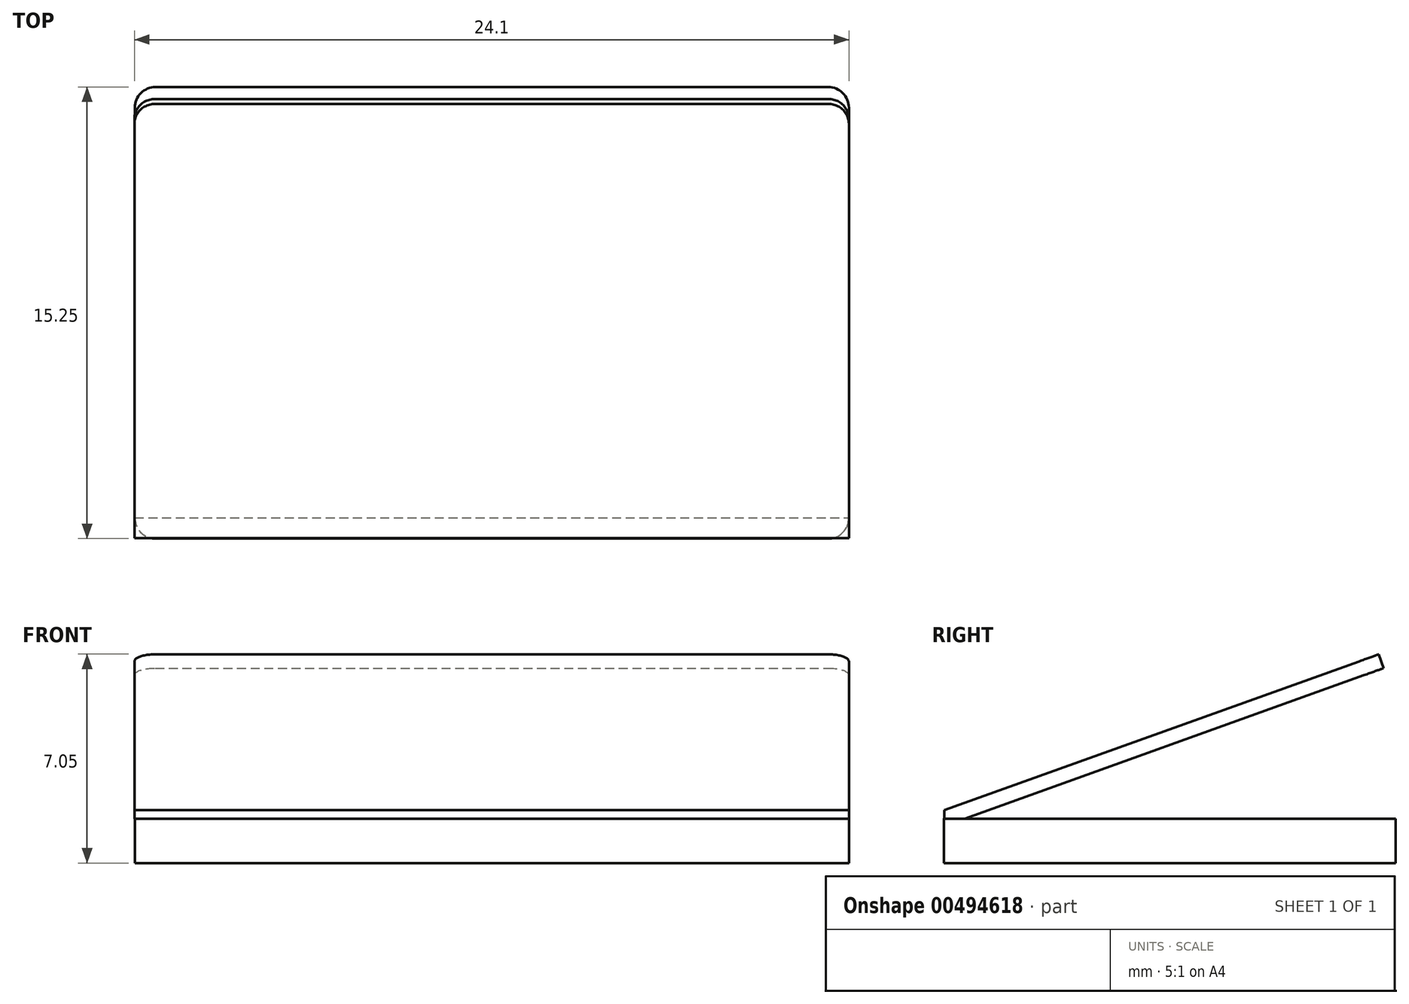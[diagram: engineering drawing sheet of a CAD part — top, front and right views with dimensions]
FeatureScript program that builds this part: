
annotation { "Feature Type Name" : "Feature", "Feature Type Description" : "" }
export const myFeature = defineFeature(function(context is Context, id is Id, definition is map)
    precondition{}
    {
        {
            var Q0;
            Q0=qCreatedBy(makeId("Top.planeOp"),FACE);
            var sketch = newSketch(context, id + "F0", { "sketchPlane" : qUnion([Q0])});
            skLineSegment(sketch, "E0.bottom", {"start": v(-32.32, 30.44) * mm, "end": v(-8.23, 30.44) * mm});
            skLineSegment(sketch, "E0.top", {"start": v(-32.32, 15.2) * mm, "end": v(-8.23, 15.2) * mm});
            skLineSegment(sketch, "E0.left", {"start": v(-32.32, 30.44) * mm, "end": v(-32.32, 15.2) * mm});
            skLineSegment(sketch, "E0.right", {"start": v(-8.23, 30.44) * mm, "end": v(-8.23, 15.2) * mm});
            skSolve(sketch);
        }
        {
            var Q0;
            Q0=makeQuery(id+"F0.imprint","IMPRINT",FACE,{"disambiguationData":[TD([[makeQuery(id+"F0.imprint","IMPRINT",EDGE,{"derivedFrom":sQuery(id+"F0.wireOp",EDGE,"E0.bottom")}),-1.0]])]});
            extrude(context, id + "F1", {"entities" : qUnion([Q0]), "depth" : 1.5 * mm, "offsetDistance" : 25 * mm});
        }
        {
            var Q0;
            Q0=makeQuery(id+"F1.opExtrude","SWEPT_EDGE",EDGE,{"disambiguationData":[OSD([sQuery(id+"F0.wireOp",EDGE,"E0.bottom"),sQuery(id+"F0.wireOp",EDGE,"E0.left")])]});
            var Q1;
            Q1=makeQuery(id+"F1.opExtrude","SWEPT_EDGE",EDGE,{"disambiguationData":[OSD([sQuery(id+"F0.wireOp",EDGE,"E0.top"),sQuery(id+"F0.wireOp",EDGE,"E0.left")])]});
            var Q2;
            Q2=makeQuery(id+"F1.opExtrude","SWEPT_EDGE",EDGE,{"disambiguationData":[OSD([sQuery(id+"F0.wireOp",EDGE,"E0.bottom"),sQuery(id+"F0.wireOp",EDGE,"E0.right")])]});
            var Q3;
            Q3=makeQuery(id+"F1.opExtrude","SWEPT_EDGE",EDGE,{"disambiguationData":[OSD([sQuery(id+"F0.wireOp",EDGE,"E0.top"),sQuery(id+"F0.wireOp",EDGE,"E0.right")])]});
            fillet(context, id + "F2", {"entities" : qUnion([Q0, Q1, Q2, Q3]), "tangentPropagation" : true, "radius" : 0.7 * mm, "defaultsChanged" : true, "vertexSettings" : [], "allowEdgeOverflow" : false});
        }
        {
            var Q0;
            Q0=makeQuery(id+"F1.opExtrude","SWEPT_FACE",FACE,{"disambiguationData":[OSD([sQuery(id+"F0.wireOp",EDGE,"E0.right")])]});
            var sketch = newSketch(context, id + "F3", { "sketchPlane" : qUnion([Q0])});
            skLineSegment(sketch, "E1", {"start": v(15.9, 1.5) * mm, "end": v(30.03, 6.58) * mm});
            skLineSegment(sketch, "E2", {"start": v(30.03, 6.58) * mm, "end": v(29.87, 7.05) * mm});
            skLineSegment(sketch, "E3", {"start": v(29.87, 7.05) * mm, "end": v(15.21, 1.78) * mm});
            skLineSegment(sketch, "E4", {"start": v(15.21, 1.78) * mm, "end": v(15.21, 1.5) * mm});
            skLineSegment(sketch, "E5", {"start": v(15.21, 1.5) * mm, "end": v(15.9, 1.5) * mm});
            skSolve(sketch);
        }
        {
            var Q0;
            Q0=makeQuery(id+"F3.imprint","IMPRINT",FACE,{"disambiguationData":[TD([[makeQuery(id+"F3.imprint","IMPRINT",EDGE,{"derivedFrom":sQuery(id+"F3.wireOp",EDGE,"E1")}),1.0]])]});
            extrude(context, id + "F4", {"entities" : qUnion([Q0]), "operationType" : NewBodyOperationType.ADD, "oppositeDirection" : true, "depth" : 24.1 * mm, "offsetDistance" : 25 * mm});
        }
        {
            var Q0;
            Q0=makeQuery(id+"F4.opExtrude","CAP_EDGE",EDGE,{"disambiguationData":[OSD([sQuery(id+"F3.wireOp",EDGE,"E2")])],"isStart":false});
            var Q1;
            Q1=makeQuery(id+"F4.opExtrude","CAP_EDGE",EDGE,{"disambiguationData":[OSD([sQuery(id+"F3.wireOp",EDGE,"E2")])],"isStart":true});
            fillet(context, id + "F5", {"entities" : qUnion([Q0, Q1]), "tangentPropagation" : true, "radius" : 0.7 * mm, "defaultsChanged" : true, "vertexSettings" : [], "allowEdgeOverflow" : false});
        }
    });
